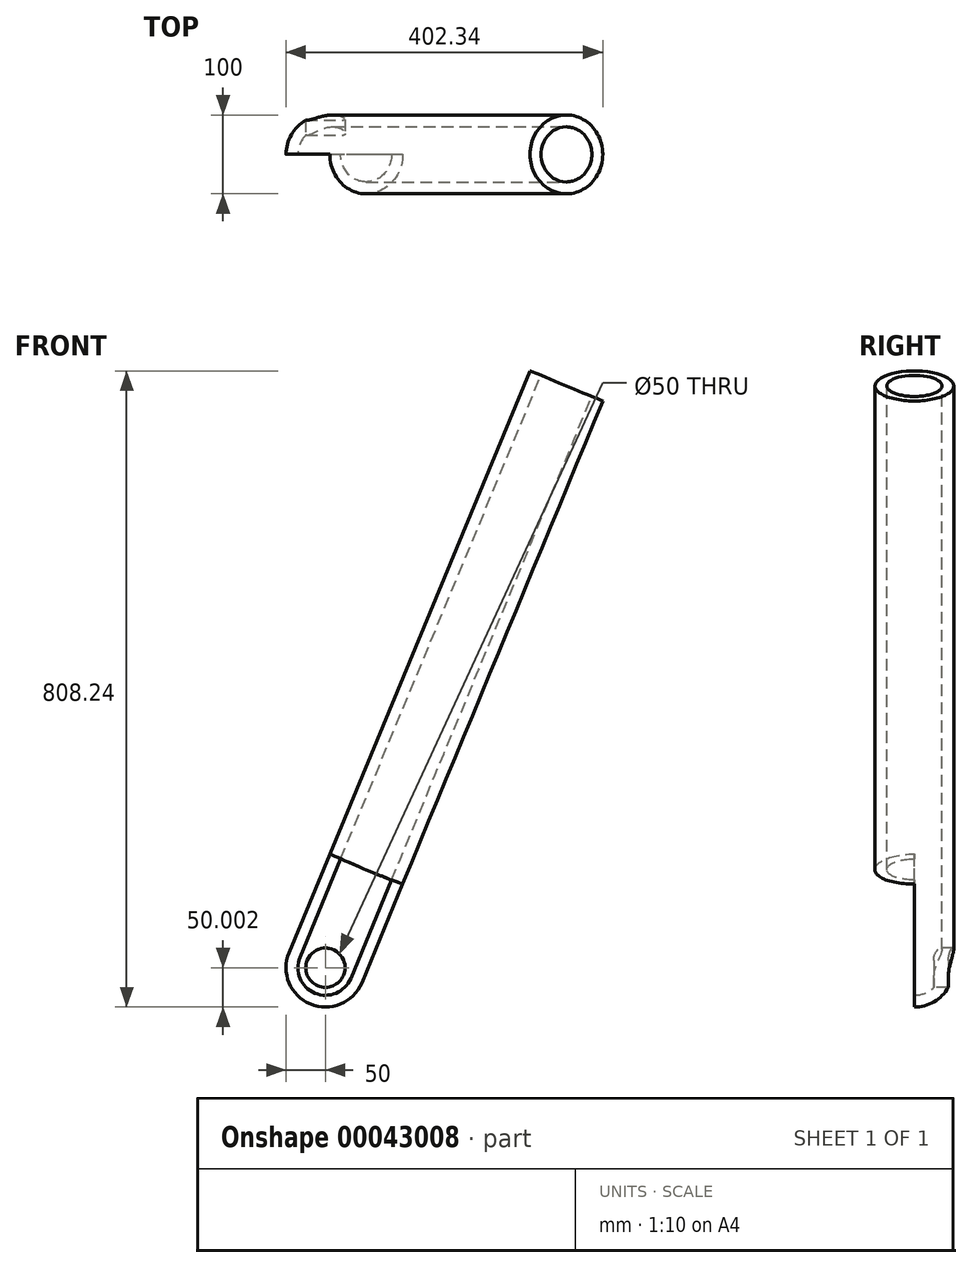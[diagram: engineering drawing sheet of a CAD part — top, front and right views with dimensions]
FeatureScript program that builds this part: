
annotation { "Feature Type Name" : "Feature", "Feature Type Description" : "" }
export const myFeature = defineFeature(function(context is Context, id is Id, definition is map)
    precondition{}
    {
        {
            var Q0;
            Q0=qCreatedBy(makeId("Front.planeOp"),FACE);
            var sketch = newSketch(context, id + "F0", { "sketchPlane" : qUnion([Q0])});
            skCircle(sketch, "E0.cCircle", {"center": v(0, 0) * mm, "radius": 1448.53 * mm, "construction": true});
            skLineSegment(sketch, "E0.0", {"start": v(600, -1448.53) * mm, "end": v(-600, -1448.53) * mm});
            skLineSegment(sketch, "E0.1", {"start": v(-600, -1448.53) * mm, "end": v(-1448.53, -600) * mm});
            skLineSegment(sketch, "E0.2", {"start": v(-1448.53, -600) * mm, "end": v(-1448.53, 600) * mm});
            skLineSegment(sketch, "E0.3", {"start": v(-1448.53, 600) * mm, "end": v(-600, 1448.53) * mm});
            skLineSegment(sketch, "E0.4", {"start": v(-600, 1448.53) * mm, "end": v(600, 1448.53) * mm});
            skLineSegment(sketch, "E0.5", {"start": v(600, 1448.53) * mm, "end": v(1448.53, 600) * mm});
            skLineSegment(sketch, "E0.6", {"start": v(1448.53, 600) * mm, "end": v(1448.53, -600) * mm});
            skLineSegment(sketch, "E0.7", {"start": v(1448.53, -600) * mm, "end": v(600, -1448.53) * mm});
            skPoint(sketch, "E0.0.midPoint", {"position": v(0, -1448.53) * mm});
            skLineSegment(sketch, "E1", {"start": v(0, 0) * mm, "end": v(-600, -1448.53) * mm});
            skLineSegment(sketch, "E2", {"start": v(0, 0) * mm, "end": v(600, -1448.53) * mm});
            skSolve(sketch);
        }
        {
            var Q0;
            Q0=qCreatedBy(makeId("Front.planeOp"),FACE);
            var sketch = newSketch(context, id + "F1", { "sketchPlane" : qUnion([Q0])});
            skLineSegment(sketch, "E3.0", {"start": v(-340.05, -690.3) * mm, "end": v(-646.2, -1429.4) * mm});
            skArc(sketch, "E4", {"start": v(-646.2, -1429.4) * mm, "mid": v(-646.2, -1467.66) * mm, "end": v(-619.13, -1494.72) * mm});
            skArc(sketch, "E5.0", {"start": v(-632.34, -1435.13) * mm, "mid": v(-632.34, -1461.92) * mm, "end": v(-613.4, -1480.86) * mm});
            skLineSegment(sketch, "E5.1", {"start": v(-326.19, -696.03) * mm, "end": v(-632.34, -1435.13) * mm});
            skLineSegment(sketch, "E6", {"start": v(-619.13, -1494.72) * mm, "end": v(-613.4, -1480.86) * mm});
            skLineSegment(sketch, "E7", {"start": v(-340.05, -690.3) * mm, "end": v(-326.19, -696.03) * mm});
            skSolve(sketch);
        }
        {
            var Q0;
            Q0 = qSketchRegion(id + "F1", true);
            var Q1;
            Q1=sQuery(id+"F0.wireOp",EDGE,"E1");
            revolve(context, id + "F2", {"entities" : qUnion([Q0]), "axis" : qUnion([Q1]), "revolveType" : RevolveType.FULL});
        }
        {
            var Q0;
            Q0=qCreatedBy(makeId("Front.planeOp"),FACE);
            var sketch = newSketch(context, id + "F3", { "sketchPlane" : qUnion([Q0])});
            skCircle(sketch, "E8", {"center": v(-600, -1448.53) * mm, "radius": 25 * mm});
            skSolve(sketch);
        }
        {
            var Q0;
            Q0 = qSketchRegion(id + "F3", true);
            extrude(context, id + "F4", {"entities" : qUnion([Q0]), "operationType" : NewBodyOperationType.REMOVE, "endBound" : BoundingType.SYMMETRIC, "oppositeDirection" : true, "depth" : 284.05 * mm});
        }
        {
            var Q0;
            Q0=qCreatedBy(makeId("Front.planeOp"),FACE);
            var sketch = newSketch(context, id + "F5", { "sketchPlane" : qUnion([Q0])});
            skCircle(sketch, "E9", {"center": v(0, 0) * mm, "radius": 1433.12 * mm});
            skCircle(sketch, "E10", {"center": v(0, 0) * mm, "radius": 1675.48 * mm});
            skSolve(sketch);
        }
        {
            var Q0;
            Q0 = qSketchRegion(id + "F5", true);
            var Q1;
            Q1=makeQuery(id+"F5.imprint","IMPRINT",FACE,{"disambiguationData":[TD([[makeQuery(id+"F5.imprint","IMPRINT",EDGE,{"derivedFrom":sQuery(id+"F5.wireOp",EDGE,"E9")}),-1.0]])]});
            extrude(context, id + "F6", {"entities" : qUnion([Q0, Q1]), "operationType" : NewBodyOperationType.REMOVE, "depth" : 100 * mm});
        }
    });
